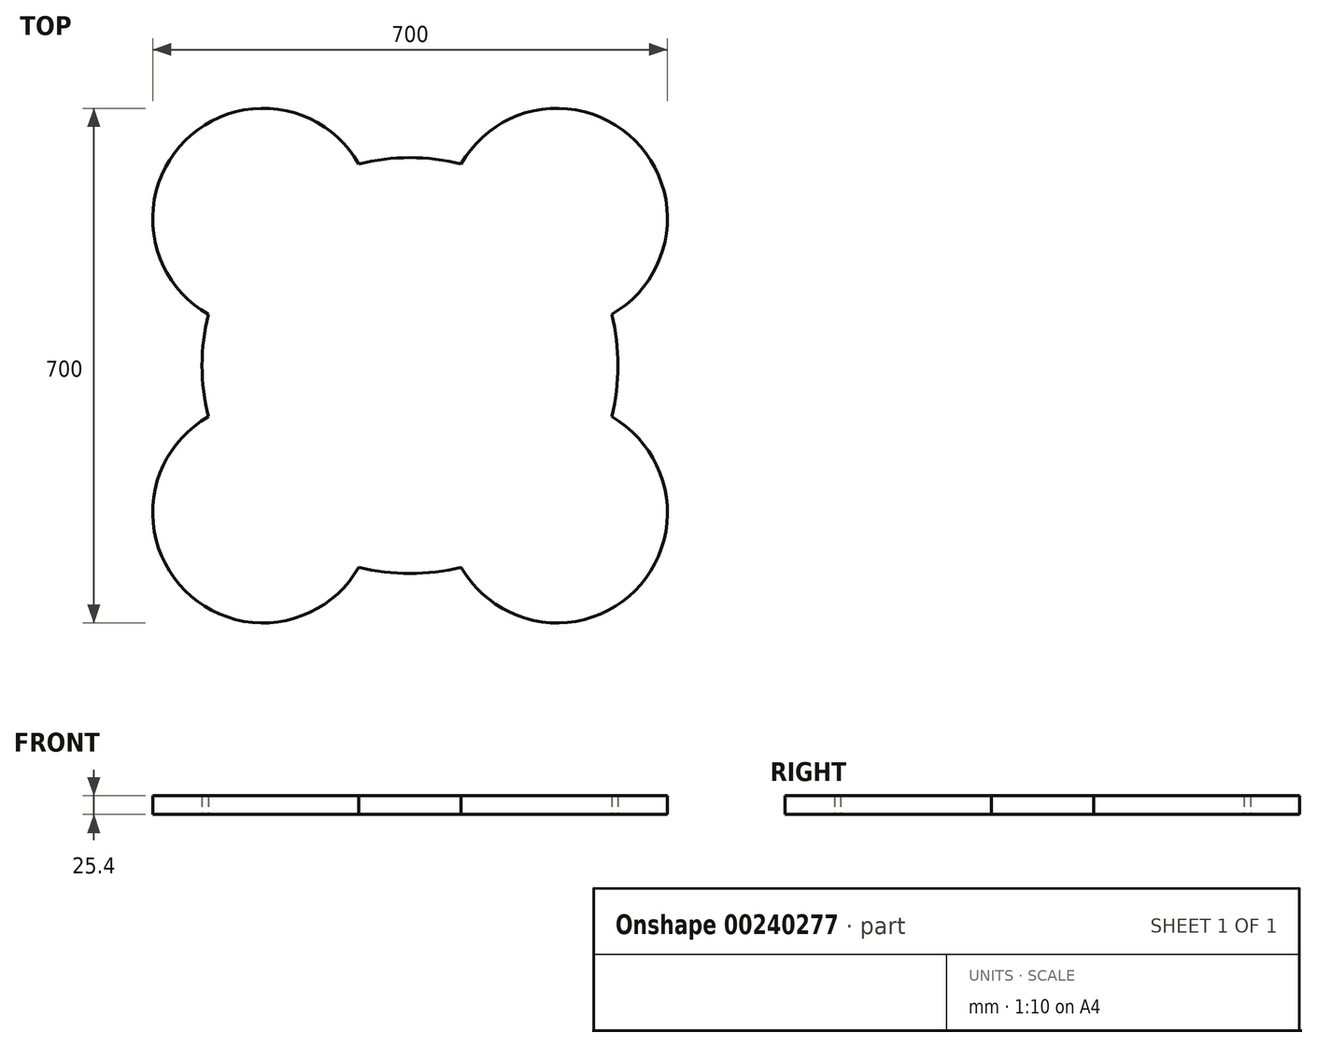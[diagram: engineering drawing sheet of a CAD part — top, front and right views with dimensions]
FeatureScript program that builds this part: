
annotation { "Feature Type Name" : "Feature", "Feature Type Description" : "" }
export const myFeature = defineFeature(function(context is Context, id is Id, definition is map)
    precondition{}
    {
        {
            var Q0;
            Q0=qCreatedBy(makeId("Top.planeOp"),FACE);
            var sketch = newSketch(context, id + "F0", { "sketchPlane" : qUnion([Q0])});
            skLineSegment(sketch, "E0.bottom", {"start": v(-200, -200) * mm, "end": v(200, -200) * mm, "construction": true});
            skLineSegment(sketch, "E0.top", {"start": v(-200, 200) * mm, "end": v(200, 200) * mm, "construction": true});
            skLineSegment(sketch, "E0.left", {"start": v(-200, -200) * mm, "end": v(-200, 200) * mm, "construction": true});
            skLineSegment(sketch, "E0.right", {"start": v(200, -200) * mm, "end": v(200, 200) * mm, "construction": true});
            skPoint(sketch, "E0.middle", {"position": v(0, 0) * mm});
            skArc(sketch, "E1", {"start": v(-274.14, 69.6) * mm, "mid": v(-282.84, 0) * mm, "end": v(-274.14, -69.6) * mm});
            skArc(sketch, "E2", {"start": v(274.14, 69.6) * mm, "mid": v(306.07, 306.07) * mm, "end": v(69.6, 274.14) * mm});
            skArc(sketch, "E3", {"start": v(-69.6, 274.14) * mm, "mid": v(-306.07, 306.07) * mm, "end": v(-274.14, 69.6) * mm});
            skArc(sketch, "E4", {"start": v(69.6, -274.14) * mm, "mid": v(306.07, -306.07) * mm, "end": v(274.14, -69.6) * mm});
            skArc(sketch, "E5", {"start": v(-274.14, -69.6) * mm, "mid": v(-306.07, -306.07) * mm, "end": v(-69.6, -274.14) * mm});
            skArc(sketch, "E6.trimOffspring", {"start": v(69.6, 274.14) * mm, "mid": v(0, 282.84) * mm, "end": v(-69.6, 274.14) * mm});
            skArc(sketch, "E7.trimOffspring", {"start": v(-69.6, -274.14) * mm, "mid": v(0, -282.84) * mm, "end": v(69.6, -274.14) * mm});
            skArc(sketch, "E8.trimOffspring", {"start": v(274.14, -69.6) * mm, "mid": v(282.84, 0) * mm, "end": v(274.14, 69.6) * mm});
            skSolve(sketch);
        }
        {
            var Q0;
            Q0=makeQuery(id+"F0.imprint","IMPRINT",FACE,{"disambiguationData":[TD([[makeQuery(id+"F0.imprint","IMPRINT",EDGE,{"derivedFrom":sQuery(id+"F0.wireOp",EDGE,"E1")}),1.0]])]});
            extrude(context, id + "F1", {"entities" : qUnion([Q0]), "depth" : 25.4 * mm});
        }
    });
